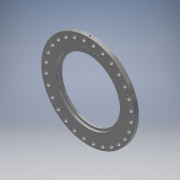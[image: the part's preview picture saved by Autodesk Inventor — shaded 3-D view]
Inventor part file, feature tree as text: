
AUTODESK INVENTOR PART (.ipt)
format: ipt  version: 2017.3 (Build 213257000, 257)  size: 310,272 bytes
history: native  units: in
note: dims shown in document units (in); Inventor stores cm internally (conversion verified against a paired STEP export)
features: sketch x6, extrude x4, chamfer x3, hole x2, pattern_circular x2, fillet x1, plane x1
ambient origin geometry x8: Origin, YZ Plane, XZ Plane, XY Plane, X Axis, Y Axis, Z Axis, Center Point
bodies: Solid1 (feature_tree)
feature tree (19):
  extrude  "Extrusion1"  Depth=1.906in TaperAngle=0.0deg
  extrude  "Extrusion2"  Depth=0.0625in TaperAngle=0.0deg
  extrude  "Extrusion3"  Depth=1.0in TaperAngle=0.0deg
  extrude  "Extrusion4"  Depth=2.0in TaperAngle=0.0deg
  hole  "Hole1"  [1 undecoded]
  chamfer  "Chamfer3"  Distance=11.0236in Angle=360.0deg
  pattern_circular  "Circular Pattern1"  Angle=45.0deg  [1 undecoded]
  chamfer  "Chamfer1"  Distance=0.0312in Angle=45.0deg
  chamfer  "Chamfer2"  Distance=0.0312in
  fillet  "Fillet2"  [1 undecoded]
  plane  "Work Plane1"
  hole  "Hole2"  [1 undecoded]
  pattern_circular  "Circular Pattern2"  [2 undecoded]
  sketch  "Sketch1"  dims[d0=43.0in d1=1.906in d2=0.0in]
  sketch  "Sketch2"  dims[d3=33.75in d4=0.0625in d5=0.0in]
  sketch  "Sketch3"  dims[d6=29.5in d7=1.0in d8=0.0in]
  sketch  "Sketch4"  dims[d9=27.5in d10=2.0in d11=0.0in]
  sketch  "Sketch5"  dims[d12=39.25in d13=0.0442in]
  sketch  "Sketch6"  dims[d14=1.875in d15=0.75in d16=0.375in d17=0.25in d18=0.5635in d19=1.0in d20=0.8108in d21=11.0236in d22=360.0deg d24=0.0625in d25=0.125in d26=45.0deg d28=0.0312in d29=0.125in d30=45.0deg d31=0.0312in d32=0.0in d33=0.0625in d34=0.125in d35=45.0deg d36=0.9688in d37=0.642in d38=2.0in d39=0.375in d40=0.25in d41=0.5635in d42=2.5in d43=0.8108in d44=0.7874in d45=360.0deg]
note: 6 required parameter values undecoded (feature->parameter linkage not recoverable at this tier; creation-order binding heuristic only, values carry confidence <= 0.55)
